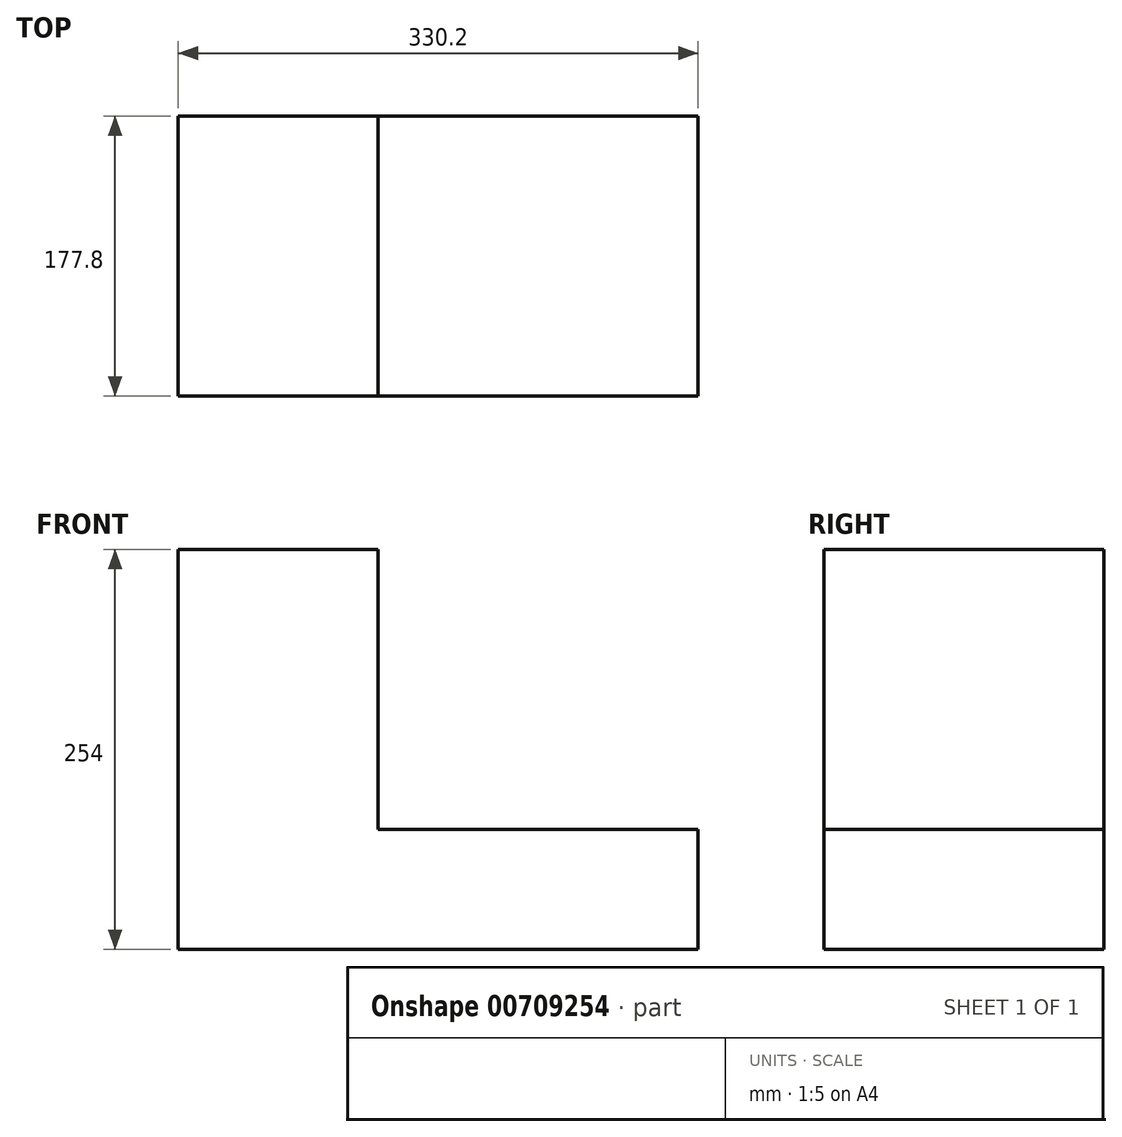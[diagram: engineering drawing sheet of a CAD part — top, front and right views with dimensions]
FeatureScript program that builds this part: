
annotation { "Feature Type Name" : "Feature", "Feature Type Description" : "" }
export const myFeature = defineFeature(function(context is Context, id is Id, definition is map)
    precondition{}
    {
        {
            var Q0;
            Q0=qCreatedBy(makeId("Front.planeOp"),FACE);
            var sketch = newSketch(context, id + "F0", { "sketchPlane" : qUnion([Q0])});
            skLineSegment(sketch, "E0.bottom", {"start": v(-189.22, 65.15) * mm, "end": v(-62.22, 65.15) * mm});
            skLineSegment(sketch, "E0.top", {"start": v(-189.22, -112.65) * mm, "end": v(-62.22, -112.65) * mm});
            skLineSegment(sketch, "E0.left", {"start": v(-189.22, 65.15) * mm, "end": v(-189.22, -112.65) * mm});
            skLineSegment(sketch, "E0.right", {"start": v(-62.22, 65.15) * mm, "end": v(-62.22, -112.65) * mm});
            skLineSegment(sketch, "E1.bottom", {"start": v(-189.22, -112.65) * mm, "end": v(140.98, -112.65) * mm});
            skLineSegment(sketch, "E1.top", {"start": v(-189.22, -188.85) * mm, "end": v(140.98, -188.85) * mm});
            skLineSegment(sketch, "E1.left", {"start": v(-189.22, -112.65) * mm, "end": v(-189.22, -188.85) * mm});
            skLineSegment(sketch, "E1.right", {"start": v(140.98, -112.65) * mm, "end": v(140.98, -188.85) * mm});
            skSolve(sketch);
        }
        {
            var Q0;
            Q0=makeQuery(id+"F0.imprint","IMPRINT",FACE,{"disambiguationData":[TD([[makeQuery(id+"F0.imprint","IMPRINT",EDGE,{"derivedFrom":sQuery(id+"F0.wireOp",EDGE,"E0.bottom")}),-1.0]])]});
            var Q1;
            Q1=makeQuery(id+"F0.imprint","IMPRINT",FACE,{"disambiguationData":[TD([[makeQuery(id+"F0.imprint","IMPRINT",EDGE,{"derivedFrom":sQuery(id+"F0.wireOp",EDGE,"E1.top")}),1.0]])]});
            extrude(context, id + "F1", {"entities" : qUnion([Q0, Q1]), "depth" : 177.8 * mm, "offsetDistance" : 25.4 * mm});
        }
    });
